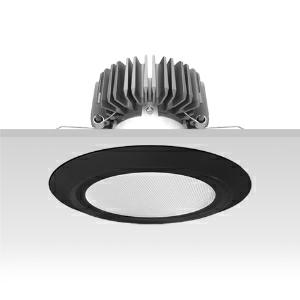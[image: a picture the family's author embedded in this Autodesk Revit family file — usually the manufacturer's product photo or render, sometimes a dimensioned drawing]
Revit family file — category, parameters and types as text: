
# Revit family: 3f_filippi_-_3f_reno_bianco_ampio_3f_filippi_-_30683_a01049_-_3f_reno_200_wh_3000-930_dali_wide___smp_bk_c546
name_source: partatom
category: Lighting Fixtures
units: mm (PartAtom-declared; Revit-internal decimal feet)

## family parameters
Cut with Voids When Loaded = No
Host = Face
Light Source = No
Part Type = Normal
Room Calculation Point = No
Round Connector Dimension = Use Diameter
Shared = No

## types (1)
- 3F Filippi - 3F Reno Bianco Ampio (1 x LED, 2320 lm, 37 W, 3000 K)
    Apparent Load = 37 VA
    Approval mark = CE
    CIE Flux Codes = 74 92 98 100 100
    Color Rendering = 90
    Color Temperature = 3000 K
    Control Gear = Electronic transformer
    Default Elevation = 1800 mm
    Description = ILLUMINOTECHNICAL
Luminous efficiency 100% (DLOR 100%, ULOR 0%).
Initial luminous flux of the luminaire 2320 lm.
Direct symmetric wide distribution.
Installation Interdistance Transv.D = 1.06 x hu - Long.D = 1.04 x hu.
Tabular UGR (CIE 117 - 4H-8H; S=0.25H; 70/50/20): RUG 22.5 - 22.3.
Beam angle: 70° - 69°.
Luminous efficacy 63 lm/W.
Lifetime (L90/B10): 30000 h. (tq+25°C)
Lifetime (L85/B10): 50000 h. (tq+25°C)
Lifetime (L70/B10): 80000 h. (tq+25°C)
Sudden decreased luminous flux after 50000 hours: 0% (C0).
Photobiological safety in compliance with IEC/TR 62778: RG0 risk exempt, (IEC 62471).
In compliance with IEC/EN 62722-2-1 - IEC/EN 62717 standards.

SOURCE
Compact LED module 3000/930.
Energy efficiency class (UE 2019/2020 - UE 2019/2015): E.
CIE 13.3 Colour rendering index: CRI >90 (R9 >50%).
IES TM-30 Fidelity Index: Rf = 92 Rg = 101.
CCT nominal colour temperature 3000 K.
Colour initial tolerance (MacAdam): SDCM 3.
Zhaga Book 3 compliant.

MECHANICAL
Passive heat dissipator in die-casting aluminium, oversized, for optimum thermal management of the LED module.
Parabolic element with graduated/concentric rings in white polycarbonate.
Transparent external lens with glossy and satin differentiated surfaces, with a cooling and anti-insect system in methacrylate (PMMA).
Fastening spring clips in stainless steel.
Dimensions: diameter 226 mm, height 146 mm. Weight 1.695 kg.
IP44 protection degree for exposed part, IP20 for recessed part.
Mechanical strength to impacts IK05 (0.7 joule).
Glow-wire test resistance 650°C.

ELECTRICAL
Wiring on a separate unit.
Halogen Free DALI-2 DATI (Parts 251, 252, 253), PUSH-DIM, electronic wiring 230V-50/60Hz, power factor 0.97 at full load, THD <25%, constant output current, SELV, class II, 1 driver, 1 DALI addresse.
Power of the luminaire 37 W.
ENEC - CE.
SAFE FLICKER: PstLM=<1 and SVM=<0.4 (IEC TR 61547-1 and IEC TR 63158), to ensure a more comfortable and safe light.
Luminaire compliant with EN 60598-2-22 for power supply from a centralised emergency system CPSS (Central Power Supply System), not incorporated in the luminaire - high risk areas excluded. The default power and flux are 100% in AC and 100% in DC.
Ambient temperature from 0°C to +25°C.
Temperature class T6 max 85°C.
Relative humidity UR: <85%.

INSTALLATION
Pull-up recessed fitting.
False ceiling carving: 200 mm.
All accessories dedicated to this product are available on the Catalog and on our website www.3F-Filippi.com.

ACCESSORIES
A01049 - Anti-glare microprismatic SMP diffuser in methacrylate (PMMA), locked and in line with the trim, in black polycarbonate.

APPLICATIONS
Suitable product for food production plants (HACCP), IFS (Food Version 6), BRC (GSFS Food Version 7).
Environments: architectural, commercial, exhibition areas, transit areas, corridors, shops, display windows, service areas.
In false ceilings with narrow voids.

LIGHT MANAGEMENT
Recommended minimum setting: 10%.
The luminaire, equipped with (DALI-2 DATI) driver, can be controlled manually with 3F Easy Dim technology or automatically/manually with wired or wireless DALI/D2D control systems.
The D2D driver guarantees interoperability with other devices with the same certification by making the following information available:
Device Data (Part 251), Energy Report (Part 252), Diagnosis & Maintenance (Part 253).
In electrical systems without a regulation system (manual or automatic) and DALI bus, a suitable jumper must be made on the DA-DA terminals of the appliance.

WARNING
Luminaire designed for disposal/recycling at end-of-life.
Replaceable (LED only) light source by a professional. Replaceable control gear by a professional.
    Height = 0 mm  [stored 0 ft]
    Lamp = 1 x LED
    Lamp Light Flux = 2320 lm
    Lamp Power = 37 W
    Lamp count = 1
    Length = 226 mm
    Lifetime = 50000 h
    Luminous efficacy = 63 lm/W
    Manufacturer = 3F Filippi
    ModVariant = No
    Model = 3F Filippi - 30683+A01049 - 3F Reno 200 WH 3000-930 DALI WIDE + SMP BK
    Mounting Place = Ceiling
    Mounting Type = Recessed
    Number of Poles = 1
    OnlyDefault = Yes
    Power Factor = 1
    Product Name = 3F Filippi - 3F Reno Bianco Ampio
    Product group = recessed luminaire
    ProductGroupID = 4
    Protection Class = Protection class II
    Protection Degree = IP 20
    RLX_Detail_Level = 1
    RLX_Emergency_Light_Flux = 0 lm
    RLX_Emergency_Type = 0
    RLX_Emergency_Type_DB = No
    RlxData = <blob elided: 99857 chars, md5=af8a70b7>
    Socket = socket
    Standby Power = 0 W
    System Light Flux = 2320 lm
    System Power = 37 W
    Type Comments = Product without accessories
    Type Image = 3ffilippi_3f_reno_200_bk_vs_smp.jpg
    URL = http://relux.com
    VarID = ---
    Voltage = 0 V
    Weight = 0.00 kg
    Width = 0 mm  [stored 0 ft]

note: [stored X ft] marks values corroborated as IEEE doubles in the binary element streams (Revit-internal decimal feet)

## geometry (parser evidence)
native form markers: Blend x4, Sweep x10
no freeform markers — native parametric forms only
